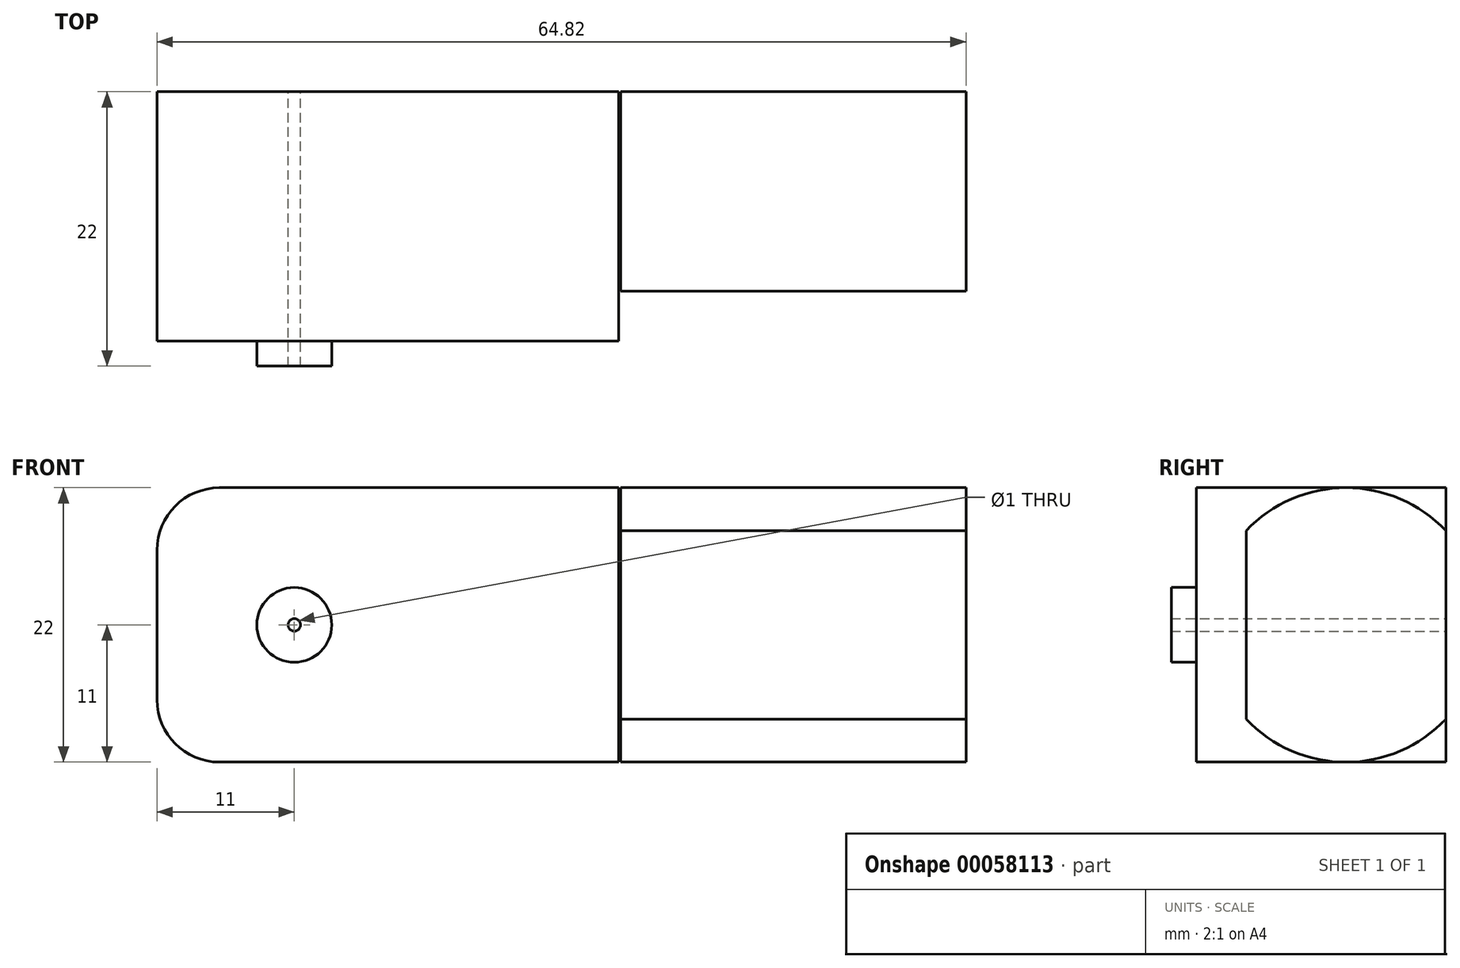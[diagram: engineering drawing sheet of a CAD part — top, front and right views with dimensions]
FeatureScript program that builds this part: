
annotation { "Feature Type Name" : "Feature", "Feature Type Description" : "" }
export const myFeature = defineFeature(function(context is Context, id is Id, definition is map)
    precondition{}
    {
        {
            var Q0;
            Q0=qCreatedBy(makeId("Front.planeOp"),FACE);
            var sketch = newSketch(context, id + "F0", { "sketchPlane" : qUnion([Q0])});
            skLineSegment(sketch, "E0.bottom", {"start": v(-41.82, 11) * mm, "end": v(-9.82, 11) * mm});
            skLineSegment(sketch, "E0.top", {"start": v(-41.82, -11) * mm, "end": v(-9.82, -11) * mm});
            skLineSegment(sketch, "E0.left", {"start": v(-46.82, 6) * mm, "end": v(-46.82, -6) * mm});
            skLineSegment(sketch, "E0.right", {"start": v(-9.82, 11) * mm, "end": v(-9.82, -11) * mm});
            skPoint(sketch, "E1.visualSharp", {"position": v(-46.82, 11) * mm});
            skArc(sketch, "E1.filletArc", {"start": v(-41.82, 11) * mm, "mid": v(-45.36, 9.54) * mm, "end": v(-46.82, 6) * mm});
            skPoint(sketch, "E2.visualSharp", {"position": v(-46.82, -11) * mm});
            skArc(sketch, "E2.filletArc", {"start": v(-46.82, -6) * mm, "mid": v(-45.36, -9.54) * mm, "end": v(-41.82, -11) * mm});
            skCircle(sketch, "E3", {"center": v(-35.82, 0) * mm, "radius": 0.5 * mm});
            skCircle(sketch, "E4", {"center": v(-35.82, 0) * mm, "radius": 3 * mm});
            skSolve(sketch);
        }
        {
            var Q0;
            Q0=makeQuery(id+"F0.imprint","IMPRINT",FACE,{"disambiguationData":[TD([[makeQuery(id+"F0.imprint","IMPRINT",EDGE,{"derivedFrom":sQuery(id+"F0.wireOp",EDGE,"E0.bottom")}),-1.0]])]});
            extrude(context, id + "F1", {"entities" : qUnion([Q0]), "depth" : 20 * mm});
        }
        {
            var Q0;
            Q0=makeQuery(id+"F0.imprint","IMPRINT",FACE,{"disambiguationData":[TD([[makeQuery(id+"F0.imprint","IMPRINT",EDGE,{"derivedFrom":sQuery(id+"F0.wireOp",EDGE,"E3")}),-1.0]])]});
            extrude(context, id + "F2", {"entities" : qUnion([Q0]), "operationType" : NewBodyOperationType.ADD, "depth" : 22 * mm});
        }
        {
            var Q0;
            Q0=qCreatedBy(makeId("Right.planeOp"),FACE);
            var sketch = newSketch(context, id + "F3", { "sketchPlane" : qUnion([Q0])});
            skLineSegment(sketch, "E5", {"start": v(-16, 7.55) * mm, "end": v(-16, -7.55) * mm});
            skArc(sketch, "E6", {"start": v(0, 7.55) * mm, "mid": v(-8, 11) * mm, "end": v(-16, 7.55) * mm});
            skArc(sketch, "E7", {"start": v(-16, -7.55) * mm, "mid": v(-8, -11) * mm, "end": v(0, -7.55) * mm});
            skLineSegment(sketch, "E8", {"start": v(0, 7.55) * mm, "end": v(0, -7.55) * mm});
            skSolve(sketch);
        }
        {
            var Q0;
            Q0=makeQuery(id+"F3.imprint","IMPRINT",FACE,{"disambiguationData":[TD([[makeQuery(id+"F3.imprint","IMPRINT",EDGE,{"derivedFrom":sQuery(id+"F3.wireOp",EDGE,"E5")}),1.0]])]});
            extrude(context, id + "F4", {"entities" : qUnion([Q0]), "operationType" : NewBodyOperationType.ADD, "oppositeDirection" : true, "depth" : 9.68 * mm});
        }
        {
            var Q0;
            Q0=makeQuery(id+"F4.opExtrude","CAP_FACE",FACE,{"disambiguationData":[OSD([sQuery(id+"F3.wireOp",EDGE,"E5"),sQuery(id+"F3.wireOp",EDGE,"E6"),sQuery(id+"F3.wireOp",EDGE,"E7"),sQuery(id+"F3.wireOp",EDGE,"E8")])],"isStart":true});
            extrude(context, id + "F5", {"entities" : qUnion([Q0]), "operationType" : NewBodyOperationType.ADD, "depth" : 18 * mm});
        }
    });
